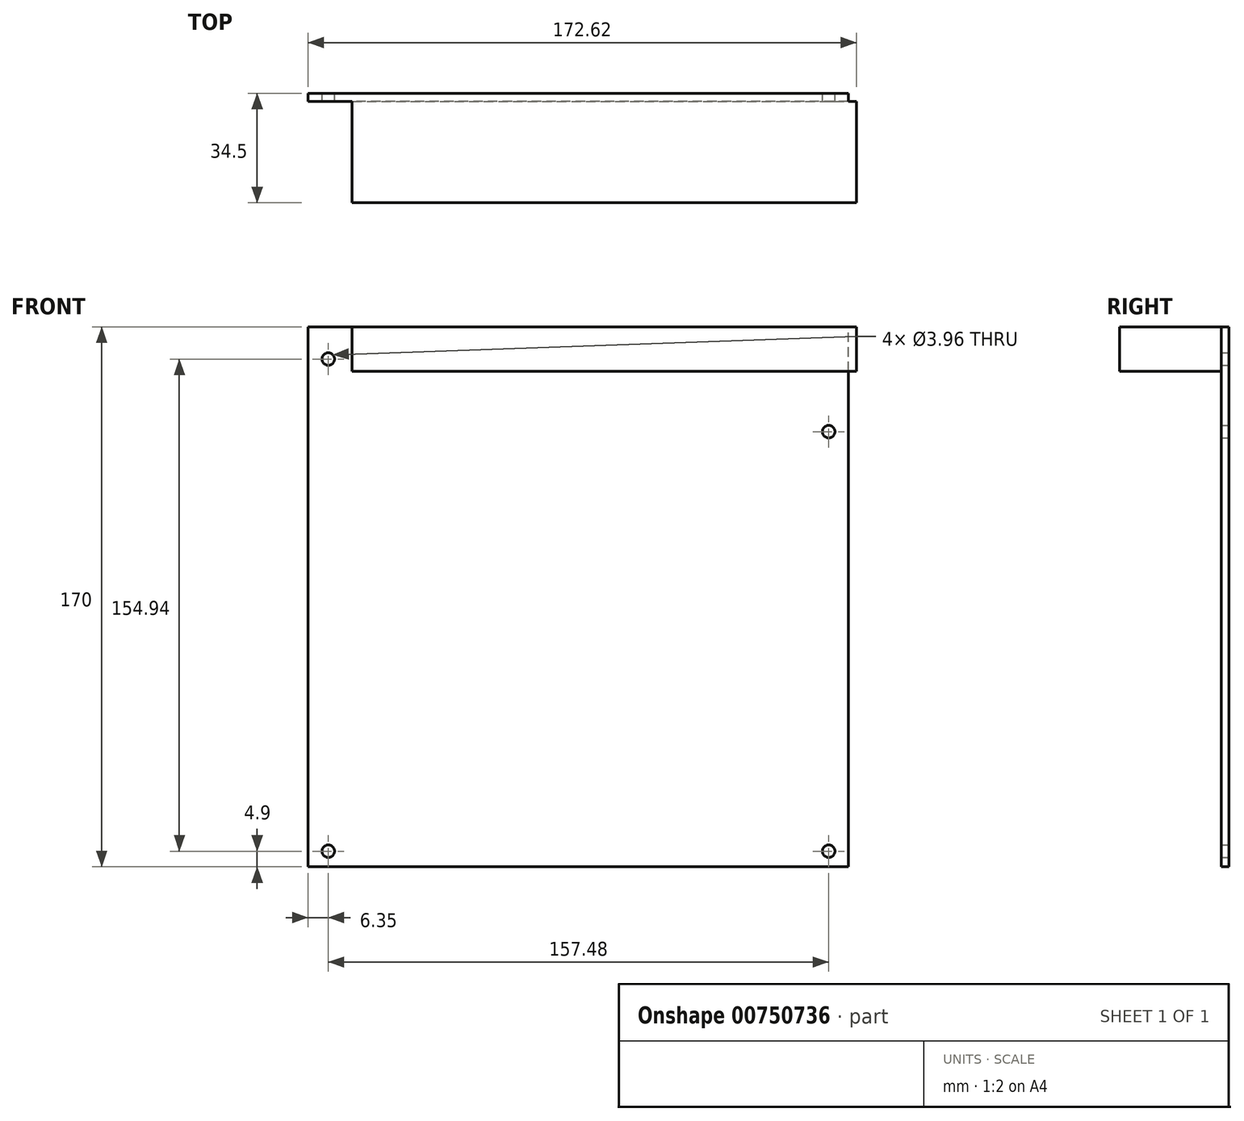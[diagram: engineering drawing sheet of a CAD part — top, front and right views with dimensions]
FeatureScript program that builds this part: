
annotation { "Feature Type Name" : "Feature", "Feature Type Description" : "" }
export const myFeature = defineFeature(function(context is Context, id is Id, definition is map)
    precondition{}
    {
        {
            var Q0;
            Q0=qCreatedBy(makeId("Front.planeOp"),FACE);
            var sketch = newSketch(context, id + "F0", { "sketchPlane" : qUnion([Q0])});
            skLineSegment(sketch, "E0.bottom", {"start": v(85, -85) * mm, "end": v(-85, -85) * mm});
            skLineSegment(sketch, "E0.top", {"start": v(85, 85) * mm, "end": v(-85, 85) * mm});
            skLineSegment(sketch, "E0.left", {"start": v(85, -85) * mm, "end": v(85, 85) * mm});
            skLineSegment(sketch, "E0.right", {"start": v(-85, -85) * mm, "end": v(-85, 85) * mm});
            skPoint(sketch, "E0.middle", {"position": v(0, 0) * mm});
            skCircle(sketch, "E1", {"center": v(-78.65, 74.84) * mm, "radius": 1.98 * mm});
            skCircle(sketch, "E2", {"center": v(78.83, 51.98) * mm, "radius": 1.98 * mm});
            skCircle(sketch, "E3", {"center": v(78.83, -80.1) * mm, "radius": 1.98 * mm});
            skCircle(sketch, "E4", {"center": v(-78.65, -80.1) * mm, "radius": 1.98 * mm});
            skLineSegment(sketch, "E5", {"start": v(-78.65, -80.1) * mm, "end": v(78.83, -80.1) * mm, "construction": true});
            skLineSegment(sketch, "E6", {"start": v(78.83, 51.98) * mm, "end": v(78.83, -80.1) * mm, "construction": true});
            skLineSegment(sketch, "E7", {"start": v(-78.65, 74.84) * mm, "end": v(85, 74.84) * mm, "construction": true});
            skLineSegment(sketch, "E8", {"start": v(-78.65, 74.84) * mm, "end": v(-78.65, -80.1) * mm, "construction": true});
            skSolve(sketch);
        }
        {
            var Q0;
            Q0 = qSketchRegion(id + "F0", true);
            extrude(context, id + "F1", {"entities" : qUnion([Q0]), "depth" : 2.5 * mm, "offsetDistance" : 25 * mm});
        }
        {
            var Q0;
            Q0=makeQuery(id+"F1.opExtrude","CAP_FACE",FACE,{"disambiguationData":[OSD([sQuery(id+"F0.wireOp",EDGE,"E0.bottom"),sQuery(id+"F0.wireOp",EDGE,"E0.top"),sQuery(id+"F0.wireOp",EDGE,"E0.left"),sQuery(id+"F0.wireOp",EDGE,"E0.right"),sQuery(id+"F0.wireOp",EDGE,"E1"),sQuery(id+"F0.wireOp",EDGE,"E2"),sQuery(id+"F0.wireOp",EDGE,"E3"),sQuery(id+"F0.wireOp",EDGE,"E4")])],"isStart":false});
            var sketch = newSketch(context, id + "F2", { "sketchPlane" : qUnion([Q0])});
            skLineSegment(sketch, "E9.bottom", {"start": v(-71.13, 85) * mm, "end": v(87.62, 85) * mm});
            skLineSegment(sketch, "E9.top", {"start": v(-71.13, 70.99) * mm, "end": v(87.62, 70.99) * mm});
            skLineSegment(sketch, "E9.left", {"start": v(-71.13, 85) * mm, "end": v(-71.13, 70.99) * mm});
            skLineSegment(sketch, "E9.right", {"start": v(87.62, 85) * mm, "end": v(87.62, 70.99) * mm});
            skSolve(sketch);
        }
        {
            var Q0;
            Q0 = qSketchRegion(id + "F2", true);
            extrude(context, id + "F3", {"entities" : qUnion([Q0]), "operationType" : NewBodyOperationType.ADD, "depth" : 32 * mm, "offsetDistance" : 25 * mm});
        }
    });
